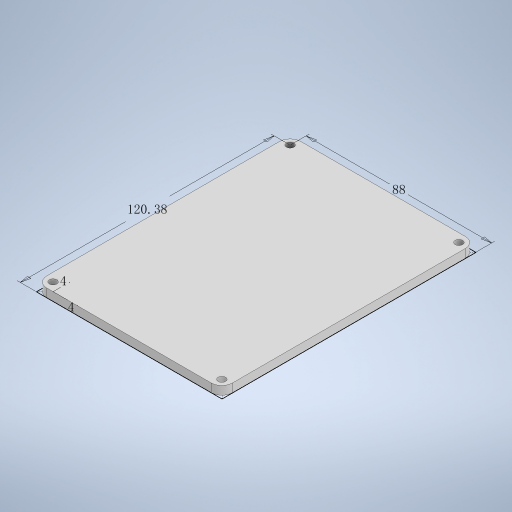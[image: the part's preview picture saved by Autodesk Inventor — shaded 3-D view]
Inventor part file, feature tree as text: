
AUTODESK INVENTOR PART (.ipt)
format: ipt  version: 2024 (Build 280153000, 153)  size: 250,368 bytes
history: native  units: mm
features: other x4, sketch x1, extrude x1, hole x1
ambient origin geometry x8: Origin, YZ Plane, XZ Plane, XY Plane, X Axis, Y Axis, Z Axis, Center Point
bodies: 实体1 (feature_tree)
feature tree (7):
  sketch  "草图1"  dims[d0=88.0mm d1=120.38mm d2=4.0mm d3=4.0mm d4=4.0mm d5=0.0mm d6=3.5mm d7=6.0mm d8=4.0mm d9=2.0mm d10=90.0deg d11=6.0mm d12=20.594885mm d13=5.0mm d14=5.0mm d15=5.0mm d16=5.0mm]
  extrude  "拉伸1"  Depth=120.38mm
  hole  "孔1"  [1 undecoded]
  other  "面圆角1"
  other  "面圆角2"
  other  "面圆角3"
  other  "面圆角4"
note: 1 required parameter value undecoded (feature->parameter linkage not recoverable at this tier; creation-order binding heuristic only, values carry confidence <= 0.55)
